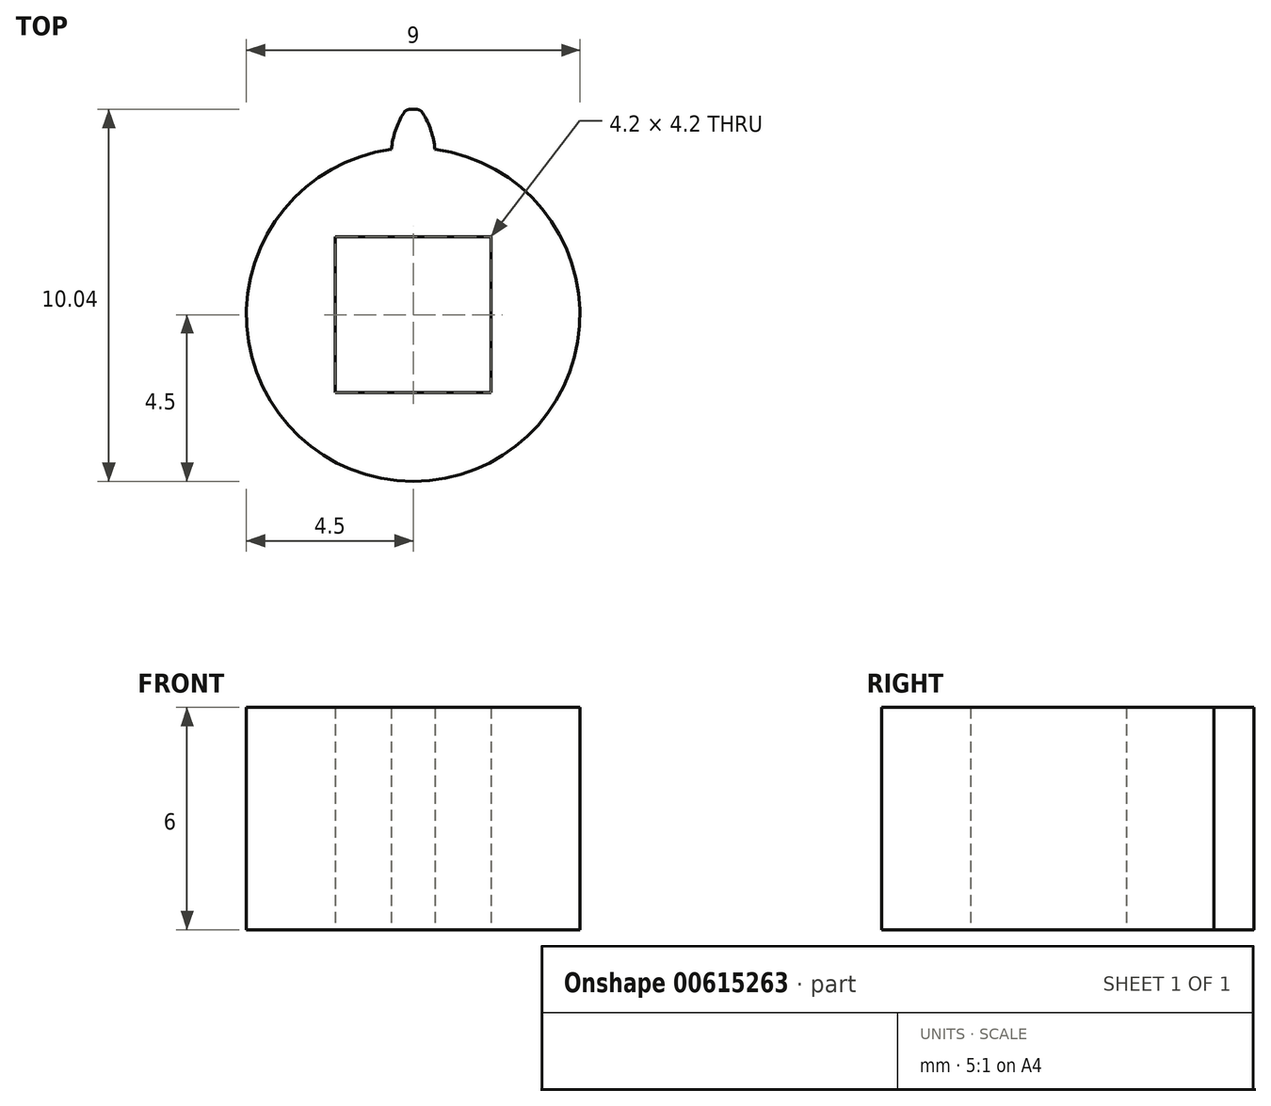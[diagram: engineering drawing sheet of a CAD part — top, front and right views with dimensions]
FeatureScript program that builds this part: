
annotation { "Feature Type Name" : "Feature", "Feature Type Description" : "" }
export const myFeature = defineFeature(function(context is Context, id is Id, definition is map)
    precondition{}
    {
        {
            var Q0;
            Q0=qCreatedBy(makeId("Top.planeOp"),FACE);
            var sketch = newSketch(context, id + "F0", { "sketchPlane" : qUnion([Q0])});
            skCircle(sketch, "E0", {"center": v(0, 0) * mm, "radius": 4.5 * mm});
            skLineSegment(sketch, "E1", {"start": v(0, 4.5) * mm, "end": v(0, -4.5) * mm, "construction": true});
            skLineSegment(sketch, "E2", {"start": v(-0.59, 4.46) * mm, "end": v(0, 0) * mm, "construction": true});
            skLineSegment(sketch, "E3", {"start": v(-1.72, 4.16) * mm, "end": v(0, 0) * mm, "construction": true});
            skLineSegment(sketch, "E4", {"start": v(-2.74, 3.57) * mm, "end": v(0, 0) * mm, "construction": true});
            skLineSegment(sketch, "E5", {"start": v(0.59, 4.46) * mm, "end": v(0, 0) * mm, "construction": true});
            skLineSegment(sketch, "E6", {"start": v(0, 0) * mm, "end": v(1.5, 4.24) * mm, "construction": true});
            skLineSegment(sketch, "E7", {"start": v(2.55, 3.7) * mm, "end": v(0, 0) * mm, "construction": true});
            skLineSegment(sketch, "E8", {"start": v(0, 0) * mm, "end": v(-3.57, 2.74) * mm, "construction": true});
            skLineSegment(sketch, "E9", {"start": v(0, 0) * mm, "end": v(3.42, 2.92) * mm, "construction": true});
            skLineSegment(sketch, "E10.bottom", {"start": v(2.1, -2.1) * mm, "end": v(-2.1, -2.1) * mm});
            skLineSegment(sketch, "E10.top", {"start": v(2.1, 2.1) * mm, "end": v(-2.1, 2.1) * mm});
            skLineSegment(sketch, "E10.left", {"start": v(2.1, -2.1) * mm, "end": v(2.1, 2.1) * mm});
            skLineSegment(sketch, "E10.right", {"start": v(-2.1, -2.1) * mm, "end": v(-2.1, 2.1) * mm});
            skLineSegment(sketch, "E11", {"start": v(-0.59, 4.46) * mm, "end": v(0.58, 4.61) * mm, "construction": true});
            skLineSegment(sketch, "E12", {"start": v(-1.72, 4.16) * mm, "end": v(0.45, 5.06) * mm, "construction": true});
            skLineSegment(sketch, "E13", {"start": v(-2.74, 3.57) * mm, "end": v(0.06, 5.72) * mm, "construction": true});
            skLineSegment(sketch, "E14", {"start": v(-3.57, 2.74) * mm, "end": v(-0.76, 6.4) * mm, "construction": true});
            skLineSegment(sketch, "E15", {"start": v(0, 4.5) * mm, "end": v(0, 5.51) * mm, "construction": true});
            skArc(sketch, "E16", {"start": v(0.59, 4.46) * mm, "mid": v(0.42, 5.13) * mm, "end": v(0.06, 5.72) * mm});
            skArc(sketch, "E17.MirrorCS", {"start": v(-0.59, 4.46) * mm, "mid": v(-0.42, 5.13) * mm, "end": v(-0.06, 5.72) * mm});
            skLineSegment(sketch, "E18", {"start": v(-0.2, 5.54) * mm, "end": v(0.2, 5.54) * mm});
            skSolve(sketch);
        }
        {
            var Q0;
            {var subQ0=sQuery(id+"F0.wireOp",EDGE,"E0");var subQ1=makeQuery(id+"F0.imprint","INTERSECT",VERTEX,{"derivedFrom":[subQ0,sQuery(id+"F0.wireOp",EDGE,"QxTWC7Lz-du55-Eq41-CNKB-dq2QVF1DEtN8")]});Q0=makeQuery(id+"F0.imprint","IMPRINT",FACE,{"disambiguationData":[TD([[makeQuery(id+"F0.imprint","IMPRINT",EDGE,{"disambiguationData":[TD([[subQ1,-1.0]])],"derivedFrom":subQ0}),1.0]])]});}
            extrude(context, id + "F1", {"entities" : qUnion([Q0]), "depth" : 6 * mm, "offsetDistance" : 25 * mm});
        }
        {
            var Q0;
            {var subQ5=sQuery(id+"F0.wireOp",EDGE,"E18");Q0=makeQuery(id+"F0.imprint","IMPRINT",FACE,{"disambiguationData":[TD([[makeQuery(id+"F0.imprint","IMPRINT",EDGE,{"derivedFrom":subQ5}),-1.0]])]});}
            extrude(context, id + "F2", {"entities" : qUnion([Q0]), "operationType" : NewBodyOperationType.ADD, "depth" : 6 * mm, "offsetDistance" : 25 * mm});
        }
        {
            var Q0;
            Q0=makeQuery(id+"F2.opExtrude","SWEPT_EDGE",EDGE,{"disambiguationData":[OSD([sQuery(id+"F0.wireOp",EDGE,"E17.MirrorCS"),sQuery(id+"F0.wireOp",EDGE,"E18")])]});
            var Q1;
            Q1=makeQuery(id+"F2.opExtrude","SWEPT_EDGE",EDGE,{"disambiguationData":[OSD([sQuery(id+"F0.wireOp",EDGE,"E0"),sQuery(id+"F0.wireOp",EDGE,"E17.MirrorCS")])]});
            var Q2;
            Q2=makeQuery(id+"F2.opExtrude","SWEPT_EDGE",EDGE,{"disambiguationData":[OSD([sQuery(id+"F0.wireOp",EDGE,"E16"),sQuery(id+"F0.wireOp",EDGE,"E18")])]});
            var Q3;
            Q3=makeQuery(id+"F2.opExtrude","SWEPT_EDGE",EDGE,{"disambiguationData":[OSD([sQuery(id+"F0.wireOp",EDGE,"E0"),sQuery(id+"F0.wireOp",EDGE,"E16")])]});
            fillet(context, id + "F3", {"entities" : qUnion([Q0, Q1, Q2, Q3]), "radius" : .2 * mm, "tangentPropagation" : true, "allowEdgeOverflow" : false});
        }
    });
